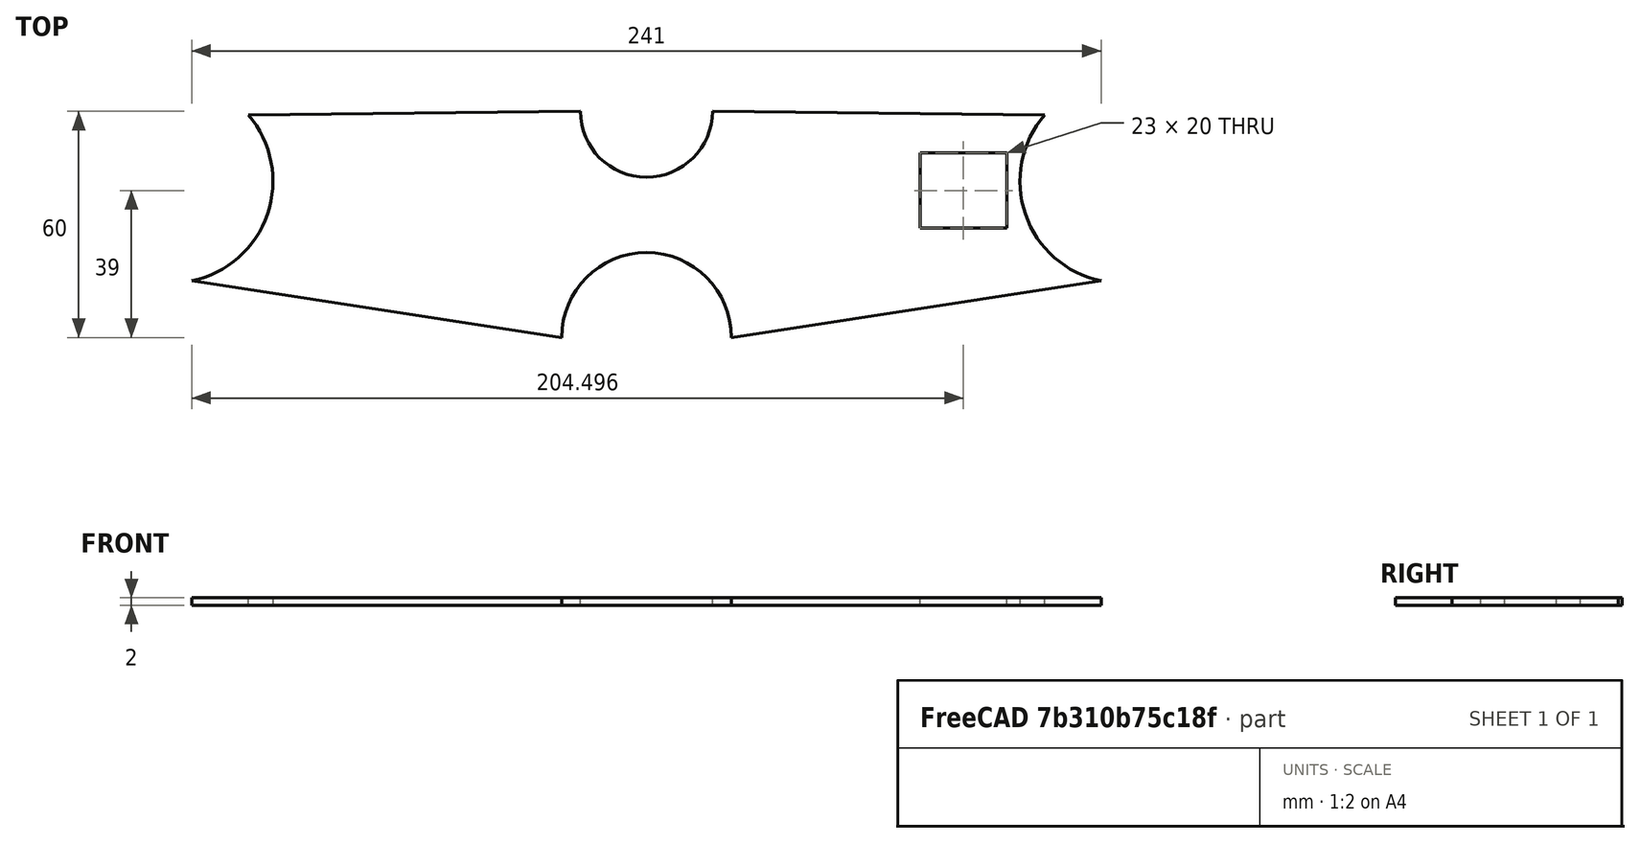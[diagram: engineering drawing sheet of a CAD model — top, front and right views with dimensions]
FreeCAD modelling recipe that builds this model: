
FCSTD DOCUMENT  (FreeCAD 0.18R16093 +53 (Git))
Label: ProtectorTijaCBR
License: All rights reserved
LicenseURL: http://en.wikipedia.org/wiki/All_rights_reserved
objects: Sketcher::SketchObject×1, PartDesign::Pad×1, PartDesign::Body×1
note: 4 computed .brp shape members not serialized (recipe doc carries the construction recipe); baked Part::Feature solids carry a one-line shape summary decoded from their .brp

FEATURE [Sketcher::SketchObject] Sketch
  MapMode = 5
  Support = -> [XY_Plane]
  sketch-geometry (12):
    g0: LineSegment StartX=-105.496 StartY=53 StartZ=0 EndX=-17.5 EndY=54 EndZ=0
    g1: LineSegment StartX=17.5 StartY=54 StartZ=0 EndX=105.496 EndY=53 EndZ=0
    g2: LineSegment StartX=120.496 StartY=9 StartZ=0 EndX=22.5 EndY=-6 EndZ=0
    g3: LineSegment StartX=-22.5 StartY=-6 StartZ=0 EndX=-120.496 EndY=9 EndZ=0
    g4: ArcOfCircle CenterX=-126 CenterY=35.4331 CenterZ=0 NormalX=0 NormalY=0 NormalZ=1 AngleXU=0 Radius=27 StartAngle=4.91767 EndAngle=6.99159
    g5: ArcOfCircle CenterX=126 CenterY=35.4331 CenterZ=0 NormalX=0 NormalY=0 NormalZ=1 AngleXU=0 Radius=27 StartAngle=2.43318 EndAngle=4.50711
    g6: ArcOfCircle CenterX=1.1e-15 CenterY=54 CenterZ=0 NormalX=0 NormalY=0 NormalZ=1 AngleXU=0 Radius=17.5 StartAngle=3.14159 EndAngle=6.28319
    g7: ArcOfCircle CenterX=-9e-16 CenterY=-6 CenterZ=0 NormalX=0 NormalY=0 NormalZ=1 AngleXU=0 Radius=22.5 StartAngle=4.60676e-09 EndAngle=3.14159
    g8: LineSegment StartX=72.4962 StartY=43 StartZ=0 EndX=95.4962 EndY=43 EndZ=0
    g9: LineSegment StartX=95.4962 StartY=43 StartZ=0 EndX=95.4962 EndY=23 EndZ=0
    g10: LineSegment StartX=95.4962 StartY=23 StartZ=0 EndX=72.4962 EndY=23 EndZ=0
    g11: LineSegment StartX=72.4962 StartY=23 StartZ=0 EndX=72.4962 EndY=43 EndZ=0
  constraints (36):
    c: Coincident(g4,g0)
    c: Coincident(g1,g5)
    c: Coincident(g5,g2)
    c: Coincident(g3,g4)
    c: Symmetric(g3,g2,g-2)
    c: Symmetric(g0,g1,g-2)
    c: DistanceX(g4,g-1) = 126
    c: Coincident(g6,g0)
    c: Coincident(g6,g1)
    c: Symmetric(g0,g1,g-2)
    c: Coincident(g7,g3)
    c: Coincident(g7,g2)
    c: Symmetric(g3,g2,g-2)
    c: DistanceY(g2,g1) = 44
    c: DistanceY(g2,g1) = 60
    c: Radius(g5) = 27
    c: Radius(g4) = 27
    c: DistanceY(g-1,g6) = 54
    c: DistanceX(g3,g2) = 45
    c: DistanceX(g0,g1) = 35
    c: Radius(g7) = 22.5
    c: Radius(g6) = 17.5
    c: DistanceX(g3,g0) = 15
    c: DistanceY(g2,g2) = 15
    c: Coincident(g8,g9)
    c: Coincident(g9,g10)
    c: Coincident(g10,g11)
    c: Coincident(g11,g8)
    c: Horizontal(g8)
    c: Horizontal(g10)
    c: Vertical(g9)
    c: Vertical(g11)
    c: DistanceY(g11,g11) = 20
    c: DistanceX(g10,g10) = 23
    c: DistanceY(g8,g1) = 10
    c: DistanceX(g8,g1) = 10
FEATURE [PartDesign::Pad] Pad
  Length = 2
  Length2 = 100
  Profile = -> Sketch
  Type = 0
FEATURE [PartDesign::Body] Body
  Group = -> [Sketch,Pad]
  Origin = -> Origin
  Tip = -> Pad
